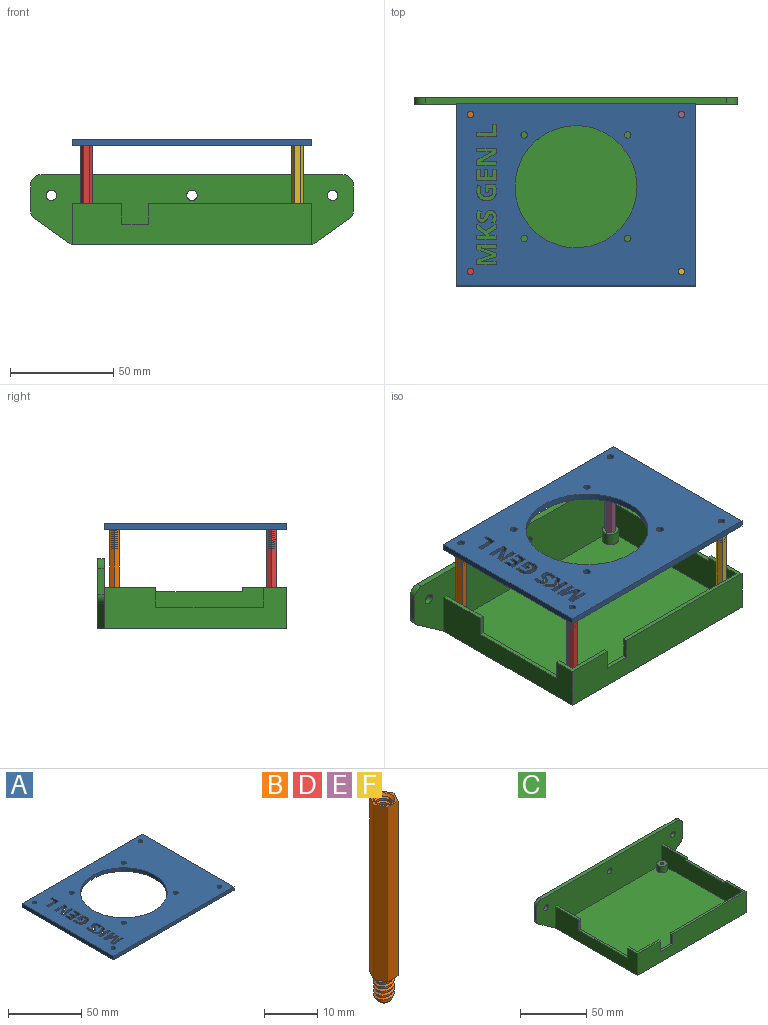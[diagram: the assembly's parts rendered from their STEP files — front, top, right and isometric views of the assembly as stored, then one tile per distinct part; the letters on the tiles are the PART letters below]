
ASSEMBLY  parts=6 mates=3
PART A: 126 faces, bbox 116x88x3 mm
  f0: plane 116x88mm, normal (0,0,1), area 7127.4mm2, adj f2,f3,f4,f5,f6,f7,f8,f9
  f1: plane 116x88mm, normal (0,0,-1), area 7127.4mm2, adj f2,f3,f4,f5,f6,f7,f8,f9
  f2: plane 88x3mm, normal (-1,0,0), area 264mm2, adj f0,f1,f3,f5
  f3: plane 116x3mm, normal (0,-1,0), area 348mm2, adj f0,f1,f2,f4
  f4: plane 88x3mm, normal (1,0,0), area 264mm2, adj f0,f1,f3,f5
  f5: plane 116x3mm, normal (0,1,0), area 348mm2, adj f0,f1,f2,f4
  f6: cylinder r=1.6mm len=3.2mm, axis (0,0,1), area 30.2mm2, adj f0,f1
  f7: cylinder r=1.6mm len=3.2mm, axis (0,0,1), area 30.2mm2, adj f0,f1
  f8: cylinder r=1.6mm len=3.2mm, axis (0,0,1), area 30.2mm2, adj f0,f1
  f9: cylinder r=1.6mm len=3.2mm, axis (0,0,1), area 30.2mm2, adj f0,f1
  f10: cylinder r=1.6mm len=3.2mm, axis (0,0,1), area 30.2mm2, adj f0,f1
  f11: cylinder r=1.6mm len=3.2mm, axis (0,0,1), area 30.2mm2, adj f0,f1
  f12: cylinder r=1.6mm len=3.2mm, axis (0,0,1), area 30.2mm2, adj f0,f1
  f13: cylinder r=1.6mm len=3.2mm, axis (0,0,1), area 30.2mm2, adj f0,f1
  f14: cylinder r=29.5mm len=59mm, axis (0,0,1), area 556.1mm2, adj f0,f1
  f15: plane 5.75x3mm, normal (-1,0,0), area 17.2mm2, adj f0,f1,f16,f18
  f16: plane 3x1.63mm, normal (0,-1,0), area 4.9mm2, adj f0,f1,f15,f17
  f17: plane 3.77x3mm, normal (1,0,0), area 11.3mm2, adj f0,f1,f16,f19
  f18: plane 9.31x3mm, normal (0,1,0), area 27.9mm2, adj f0,f1,f15,f20
  f19: plane 7.68x3mm, normal (0,-1,0), area 23mm2, adj f0,f1,f17,f20
  f20: plane 3x1.97mm, normal (1,0,0), area 5.9mm2, adj f0,f1,f18,f19
  f21: plane 9.31x3mm, normal (0,-1,0), area 27.9mm2, adj f0,f1,f22,f32
  f22: plane 3x1.78mm, normal (1,0,0), area 5.3mm2, adj f0,f1,f21,f23
  f23: plane 4.41x3mm, normal (0,1,0), area 13.2mm2, adj f0,f1,f22,f24
  f24: extruded ~3x2.56mm, area 7.7mm2, adj f0,f1,f23,f25
  f25: plane 3x0.05mm, normal (1,0,0), area 0.1mm2, adj f0,f1,f24,f26
  f26: plane 6.97x4.04mm, normal (0.5,-0.87,0), area 24.2mm2, adj f0,f1,f25,f27
  f27: plane 3x2.49mm, normal (1,0,0), area 7.5mm2, adj f0,f1,f26,f28
  f28: plane 9.31x3mm, normal (0,1,0), area 27.9mm2, adj f0,f1,f27,f29
  f29: plane 3x1.76mm, normal (-1,0,0), area 5.3mm2, adj f0,f1,f28,f30
  f30: plane 4.38x3mm, normal (0,-1,0), area 13.1mm2, adj f0,f1,f29,f31
  f31: extruded ~3x2.66mm, area 8mm2, adj f0,f1,f30,f33
  f32: plane 3x2.51mm, normal (-1,0,0), area 7.5mm2, adj f0,f1,f21,f34
  f33: plane 3x0.06mm, normal (-1,0,0), area 0.2mm2, adj f0,f1,f31,f34
  f34: plane 7.04x4.05mm, normal (-0.5,0.87,0), area 24.4mm2, adj f0,f1,f32,f33
  f35: plane 3x1.63mm, normal (0,-1,0), area 4.9mm2, adj f0,f1,f36,f44
  f36: plane 3.39x3mm, normal (1,0,0), area 10.2mm2, adj f0,f1,f35,f37
  f37: plane 3x2.4mm, normal (0,-1,0), area 7.2mm2, adj f0,f1,f36,f38
  f38: plane 3.15x3mm, normal (-1,0,0), area 9.5mm2, adj f0,f1,f37,f39
  f39: plane 3x1.62mm, normal (0,-1,0), area 4.9mm2, adj f0,f1,f38,f40
  f40: plane 3.15x3mm, normal (1,0,0), area 9.5mm2, adj f0,f1,f39,f41
  f41: plane 3x2.04mm, normal (0,-1,0), area 6.1mm2, adj f0,f1,f40,f42
  f42: plane 3.39x3mm, normal (-1,0,0), area 10.2mm2, adj f0,f1,f41,f43
  f43: plane 3x1.62mm, normal (0,-1,0), area 4.9mm2, adj f0,f1,f42,f45
  f44: plane 5.36x3mm, normal (-1,0,0), area 16.1mm2, adj f0,f1,f35,f46
  f45: plane 5.36x3mm, normal (1,0,0), area 16.1mm2, adj f0,f1,f43,f46
  f46: plane 9.31x3mm, normal (0,1,0), area 27.9mm2, adj f0,f1,f44,f45
  f47: plane 3x1.64mm, normal (0,1,0), area 4.9mm2, adj f0,f1,f48,f63
  f48: plane 3x1.76mm, normal (-1,0,0), area 5.3mm2, adj f0,f1,f47,f49
  f49: plane 3x1.94mm, normal (0,1,0), area 5.8mm2, adj f0,f1,f48,f50
  f50: extruded ~3x1.25mm, area 3.8mm2, adj f0,f1,f49,f51
  f51: extruded ~3x1.8mm, area 6.1mm2, adj f0,f1,f50,f52
  f52: extruded ~3x2.31mm, area 7.3mm2, adj f0,f1,f51,f53
  f53: extruded ~3x2.31mm, area 7.5mm2, adj f0,f1,f52,f54
  f54: extruded ~3x2.05mm, area 6.9mm2, adj f0,f1,f53,f55
  f55: extruded ~3x2.12mm, area 6.6mm2, adj f0,f1,f54,f56
  f56: plane 3x1.58mm, normal (-0.38,-0.92,0), area 5.1mm2, adj f0,f1,f55,f57
  f57: extruded ~3x2.76mm, area 8.5mm2, adj f0,f1,f56,f58
  f58: extruded ~3.57x3mm, area 11.7mm2, adj f0,f1,f57,f59
  f59: extruded ~3.51x3mm, area 11.5mm2, adj f0,f1,f58,f60
  f60: extruded ~3.56x3mm, area 11.4mm2, adj f0,f1,f59,f61
  f61: extruded ~3.22x3mm, area 10.7mm2, adj f0,f1,f60,f62
  f62: extruded ~3x1.62mm, area 4.9mm2, adj f0,f1,f61,f64
  f63: plane 3.69x3mm, normal (1,0,0), area 11.1mm2, adj f0,f1,f47,f65
  f64: extruded ~3x1.69mm, area 5.2mm2, adj f0,f1,f62,f65
  f65: plane 4.83x3mm, normal (0,-1,0), area 14.5mm2, adj f0,f1,f63,f64
  f66: extruded ~3x1.54mm, area 4.9mm2, adj f0,f1,f67,f91
  f67: extruded ~3x1.79mm, area 6.6mm2, adj f0,f1,f66,f68
  f68: extruded ~3x1.25mm, area 4.2mm2, adj f0,f1,f67,f69
  f69: extruded ~3x0.39mm, area 1.6mm2, adj f0,f1,f68,f70
  f70: extruded ~3x0.46mm, area 1.4mm2, adj f0,f1,f69,f71
  f71: extruded ~3x0.68mm, area 2.3mm2, adj f0,f1,f70,f72
  f72: extruded ~3x0.86mm, area 2.8mm2, adj f0,f1,f71,f73
  f73: extruded ~3x0.96mm, area 2.9mm2, adj f0,f1,f72,f74
  f74: extruded ~3x1.23mm, area 3.9mm2, adj f0,f1,f73,f75
  f75: plane 3x1.54mm, normal (-0.38,-0.92,0), area 5mm2, adj f0,f1,f74,f76
  f76: extruded ~3x1.38mm, area 4.4mm2, adj f0,f1,f75,f77
  f77: extruded ~3x1.38mm, area 4.2mm2, adj f0,f1,f76,f78
  f78: extruded ~3x2.31mm, area 7.4mm2, adj f0,f1,f77,f79
  f79: extruded ~3x1.94mm, area 6.6mm2, adj f0,f1,f78,f80
  f80: extruded ~3x1.14mm, area 3.6mm2, adj f0,f1,f79,f81
  f81: extruded ~3x0.86mm, area 3.3mm2, adj f0,f1,f80,f82
  f82: extruded ~3x1.28mm, area 4.5mm2, adj f0,f1,f81,f83
  f83: extruded ~3x1.21mm, area 4.1mm2, adj f0,f1,f82,f84
  f84: extruded ~3x0.45mm, area 1.8mm2, adj f0,f1,f83,f85
  f85: extruded ~3x0.49mm, area 1.6mm2, adj f0,f1,f84,f86
  f86: extruded ~3x0.74mm, area 2.6mm2, adj f0,f1,f85,f87
  f87: extruded ~3x1mm, area 3.1mm2, adj f0,f1,f86,f88
  f88: extruded ~3x1.19mm, area 3.6mm2, adj f0,f1,f87,f89
  f89: extruded ~3x1.59mm, area 5.1mm2, adj f0,f1,f88,f90
  f90: plane 3x1.83mm, normal (0,1,0), area 5.5mm2, adj f0,f1,f89,f92
  f91: extruded ~3x1.99mm, area 6.8mm2, adj f0,f1,f66,f93
  f92: extruded ~3x2.64mm, area 8.2mm2, adj f0,f1,f90,f93
  f93: extruded ~3x2.52mm, area 8mm2, adj f0,f1,f91,f92
  f94: plane 5.19x3.27mm, normal (0.53,-0.85,0), area 18.4mm2, adj f0,f1,f95,f104
  f95: plane 4.12x3.25mm, normal (-0.62,-0.79,0), area 15.7mm2, adj f0,f1,f94,f96
  f96: plane 3x2.19mm, normal (1,0,0), area 6.6mm2, adj f0,f1,f95,f97
  f97: plane 3.16x3mm, normal (0.62,0.78,0), area 12.1mm2, adj f0,f1,f96,f98
  f98: plane 3x1.1mm, normal (0.58,0.82,0), area 4mm2, adj f0,f1,f97,f99
  f99: plane 4.26x3mm, normal (0,-1,0), area 12.8mm2, adj f0,f1,f98,f100
  f100: plane 3x1.97mm, normal (1,0,0), area 5.9mm2, adj f0,f1,f99,f101
  f101: plane 9.31x3mm, normal (0,1,0), area 27.9mm2, adj f0,f1,f100,f102
  f102: plane 3x1.97mm, normal (-1,0,0), area 5.9mm2, adj f0,f1,f101,f103
  f103: plane 3.32x3mm, normal (0,-1,0), area 10mm2, adj f0,f1,f102,f105
  f104: plane 3x2.24mm, normal (-1,0,0), area 6.7mm2, adj f0,f1,f94,f106
  f105: plane 3x0.83mm, normal (-0.81,-0.58,0), area 3.1mm2, adj f0,f1,f103,f106
  f106: plane 3.92x3mm, normal (-0.53,0.85,0), area 13.9mm2, adj f0,f1,f104,f105
  f107: plane 3x1.81mm, normal (-1,0,0), area 5.4mm2, adj f0,f1,f108,f123
  f108: plane 7.29x3mm, normal (-0.31,-0.95,0), area 23mm2, adj f0,f1,f107,f109
  f109: plane 3x0.06mm, normal (-1,0,0), area 0.2mm2, adj f0,f1,f108,f110
  f110: extruded ~3x2.16mm, area 6.5mm2, adj f0,f1,f109,f111
  f111: extruded ~3x0.72mm, area 2.2mm2, adj f0,f1,f110,f112
  f112: plane 4.41x3mm, normal (0,1,0), area 13.2mm2, adj f0,f1,f111,f113
  f113: plane 3x1.84mm, normal (-1,0,0), area 5.5mm2, adj f0,f1,f112,f114
  f114: plane 9.31x3mm, normal (0,-1,0), area 27.9mm2, adj f0,f1,f113,f115
  f115: plane 3x2.68mm, normal (1,0,0), area 8.1mm2, adj f0,f1,f114,f116
  f116: plane 7.12x3mm, normal (0.31,0.95,0), area 22.5mm2, adj f0,f1,f115,f117
  f117: plane 3x0.04mm, normal (1,0,0), area 0.1mm2, adj f0,f1,f116,f118
  f118: plane 7.12x3mm, normal (0.3,-0.96,0), area 22.3mm2, adj f0,f1,f117,f119
  f119: plane 3x2.69mm, normal (1,0,0), area 8.1mm2, adj f0,f1,f118,f120
  f120: plane 9.31x3mm, normal (0,1,0), area 27.9mm2, adj f0,f1,f119,f121
  f121: plane 3x1.76mm, normal (-1,0,0), area 5.3mm2, adj f0,f1,f120,f122
  f122: plane 4.33x3mm, normal (0,-1,0), area 13mm2, adj f0,f1,f121,f124
  f123: plane 7.3x3mm, normal (-0.29,0.96,0), area 22.9mm2, adj f0,f1,f107,f125
  f124: extruded ~3x2.97mm, area 8.9mm2, adj f0,f1,f122,f125
  f125: plane 3x0.06mm, normal (-1,0,0), area 0.2mm2, adj f0,f1,f123,f124
PART B: 20 faces, bbox 5.6x4.9x46.5 mm
  f0: cylinder r=1.5mm len=9.5mm, axis (0,0,1), area 55.3mm2, adj f9,f16,f17,f18,f19
  f1: plane 40x2.35mm, normal (0.87,-0.5,0), area 108.5mm2, adj f2,f6,f7,f8
  f2: plane 40x2.35mm, normal (0.87,0.5,0), area 108.5mm2, adj f1,f3,f7,f8
  f3: plane 40x2.71mm, normal (0,1,0), area 108.5mm2, adj f2,f4,f7,f8
  f4: plane 40x2.35mm, normal (-0.87,0.5,0), area 108.5mm2, adj f3,f5,f7,f8
  f5: plane 40x2.35mm, normal (-0.87,-0.5,0), area 108.5mm2, adj f4,f6,f7,f8
  f6: plane 40x2.71mm, normal (0,-1,0), area 108.5mm2, adj f1,f5,f7,f8
  f7: plane 5.43x4.7mm, normal (0,0,1), area 6.6mm2, adj f1,f2,f3,f4,f5,f6,f16
  f8: plane 5.59x4.86mm, normal (0,0,-1), area 10.9mm2, adj f1,f2,f3,f4,f5,f6,f10,f13
  f9: plane 3x3mm, normal (0,0,1), area 7.1mm2, adj f0
  f10: cylinder r=1.5mm len=5.5mm, axis (0,0,1), area 27.7mm2, adj f8,f12,f13,f14,f15
  f11: plane 2x2mm, normal (0,0,-1), area 3.1mm2, adj f12
  f12: cone r=1mm half-angle=45deg, axis (0,0,1), area 5.6mm2, adj f10,f11
  f13: bspline ~5.58x4.46mm, area 27.8mm2, adj f8,f10,f14,f15
  f14: bspline ~5.75x4.46mm, area 29mm2, adj f8,f10,f13,f15
  f15: plane 0.5x0.43mm, normal (0,-1,0), area 0.1mm2, adj f10,f13,f14
  f16: cone r=1.5mm half-angle=45deg, axis (0,0,1), area 6.2mm2, adj f0,f7,f18,f19
  f17: plane 0.5x0.43mm, normal (0,1,0), area 0.1mm2, adj f0,f18,f19
  f18: bspline ~10.08x4.46mm, area 51.7mm2, adj f0,f16,f17,f19
  f19: bspline ~10.08x4.46mm, area 50.8mm2, adj f0,f16,f17,f18
PART C: 51 faces, bbox 156x91x34 mm
  f0: plane 24x11mm, normal (0,0,1), area 66mm2, adj f1,f2,f6,f9,f29,f47
  f1: plane 88x20mm, normal (-1,0,0), area 1266mm2, adj f0,f3,f9,f10,f11,f45,f46,f47
  f2: plane 86x18mm, normal (1,0,0), area 1054mm2, adj f0,f3,f6,f11,f12,f45,f46,f47
  f3: plane 25x2mm, normal (0,0,1), area 50mm2, adj f1,f2,f11,f46
  f4: plane 25x2mm, normal (0,0,1), area 50mm2, adj f5,f8,f11,f34
  f5: plane 86x18mm, normal (-1,0,0), area 1464mm2, adj f4,f6,f7,f11,f12,f32,f33,f34
  f6: plane 112x18mm, normal (0,1,0), area 1886mm2, adj f0,f2,f5,f7,f12,f29,f30,f31
  f7: plane 79x21mm, normal (0,0,1), area 196mm2, adj f5,f6,f8,f9,f31,f32
  f8: plane 88x20mm, normal (1,0,0), area 1676mm2, adj f4,f7,f9,f10,f11,f32,f33,f34
  f9: plane 116x20mm, normal (0,-1,0), area 2190mm2, adj f0,f1,f7,f8,f10,f29,f30,f31
  f10: plane 116x91mm, normal (0,0,-1), area 10556mm2, adj f1,f8,f9,f35,f39,f40
  f11: plane 156x34mm, normal (0,-1,0), area 4646mm2, adj f1,f2,f3,f4,f5,f8,f12,f35
  f12: plane 112x86mm, normal (0,0,1), area 9430.9mm2, adj f2,f5,f6,f11,f13,f15,f17,f19
  f13: cylinder r=4mm len=8mm, axis (0,0,-1), area 150.8mm2, adj f12,f14
  f14: plane 8x8mm, normal (0,0,1), area 43.7mm2, adj f13,f27
  f15: cylinder r=4mm len=8mm, axis (0,0,-1), area 150.8mm2, adj f12,f16
  f16: plane 8x8mm, normal (0,0,1), area 43.7mm2, adj f15,f25
  f17: cylinder r=4mm len=8mm, axis (0,0,-1), area 150.8mm2, adj f12,f18
  f18: plane 8x8mm, normal (0,0,1), area 43.7mm2, adj f17,f23
  f19: cylinder r=4mm len=8mm, axis (0,0,-1), area 150.8mm2, adj f12,f20
  f20: plane 8x8mm, normal (0,0,1), area 43.7mm2, adj f19,f21
  f21: cylinder r=1.45mm len=6mm, axis (0,0,1), area 54.7mm2, adj f20,f22
  f22: plane 2.9x2.9mm, normal (0,0,1), area 6.6mm2, adj f21
  f23: cylinder r=1.45mm len=6mm, axis (0,0,1), area 54.7mm2, adj f18,f24
  f24: plane 2.9x2.9mm, normal (0,0,1), area 6.6mm2, adj f23
  f25: cylinder r=1.45mm len=6mm, axis (0,0,1), area 54.7mm2, adj f16,f26
  f26: plane 2.9x2.9mm, normal (0,0,1), area 6.6mm2, adj f25
  f27: cylinder r=1.45mm len=6mm, axis (0,0,1), area 54.7mm2, adj f14,f28
  f28: plane 2.9x2.9mm, normal (0,0,1), area 6.6mm2, adj f27
  f29: plane 10x2mm, normal (1,0,0), area 20mm2, adj f0,f6,f9,f30
  f30: plane 13x2mm, normal (0,0,1), area 26mm2, adj f6,f9,f29,f31
  f31: plane 10x2mm, normal (-1,0,0), area 20mm2, adj f6,f7,f9,f30
  f32: plane 2x2mm, normal (0,1,0), area 4mm2, adj f5,f7,f8,f33
  f33: plane 42x2mm, normal (0,0,1), area 84mm2, adj f5,f8,f32,f34
  f34: plane 2x2mm, normal (0,-1,0), area 4mm2, adj f4,f5,f8,f33
  f35: plane 17.87x12.51mm, normal (-0.57,0,-0.82), area 65.4mm2, adj f10,f11,f40,f41
  f36: plane 12.4x3mm, normal (-1,0,0), area 37.2mm2, adj f11,f40,f41,f42
  f37: plane 146x3mm, normal (0,0,1), area 438mm2, adj f11,f40,f42,f43
  f38: plane 12.4x3mm, normal (1,0,0), area 37.2mm2, adj f11,f40,f43,f44
  f39: plane 17.87x12.51mm, normal (0.57,0,-0.82), area 65.4mm2, adj f10,f11,f40,f44
  f40: plane 156x34mm, normal (0,1,0), area 4950mm2, adj f10,f35,f36,f37,f38,f39,f41,f42
  f41: cylinder r=5mm len=4.1mm, axis (0,-1,0), area 14.4mm2, adj f11,f35,f36,f40
  f42: cylinder r=5mm len=5mm, axis (0,1,0), area 23.6mm2, adj f11,f36,f37,f40
  f43: cylinder r=5mm len=5mm, axis (0,-1,0), area 23.6mm2, adj f11,f37,f38,f40
  f44: cylinder r=5mm len=4.1mm, axis (0,-1,0), area 14.4mm2, adj f11,f38,f39,f40
  f45: plane 52x2mm, normal (0,0,1), area 104mm2, adj f1,f2,f46,f47
  f46: plane 9.5x2mm, normal (0,-1,0), area 19mm2, adj f1,f2,f3,f45
  f47: plane 9.5x2mm, normal (0,1,0), area 19mm2, adj f0,f1,f2,f45
  f48: cylinder r=2.55mm len=5.1mm, axis (0,-1,0), area 48.1mm2, adj f11,f40
  f49: cylinder r=2.55mm len=5.1mm, axis (0,-1,0), area 48.1mm2, adj f11,f40
  f50: cylinder r=2.55mm len=5.1mm, axis (0,-1,0), area 48.1mm2, adj f11,f40
PART D: same geometry as B
PART E: same geometry as B
PART F: same geometry as B
PLACE A t=(0,0,1.2)mm
PLACE B t=(-51,38,8)mm
PLACE C at identity
PLACE D t=(-51,-38,8.2)mm
PLACE E t=(51,38,8)mm
PLACE F t=(51,-38,9.2)mm
MATE fastened E.f10 <-> C.f17  axis (0,0,-1) through (51,38,2)mm
MATE fastened B.f10 <-> C.f15  axis (0,0,-1) through (-51,38,2)mm
MATE fastened A.f6 <-> D.f0  axis (0,0,-1) through (-51,-38,48.2)mm
